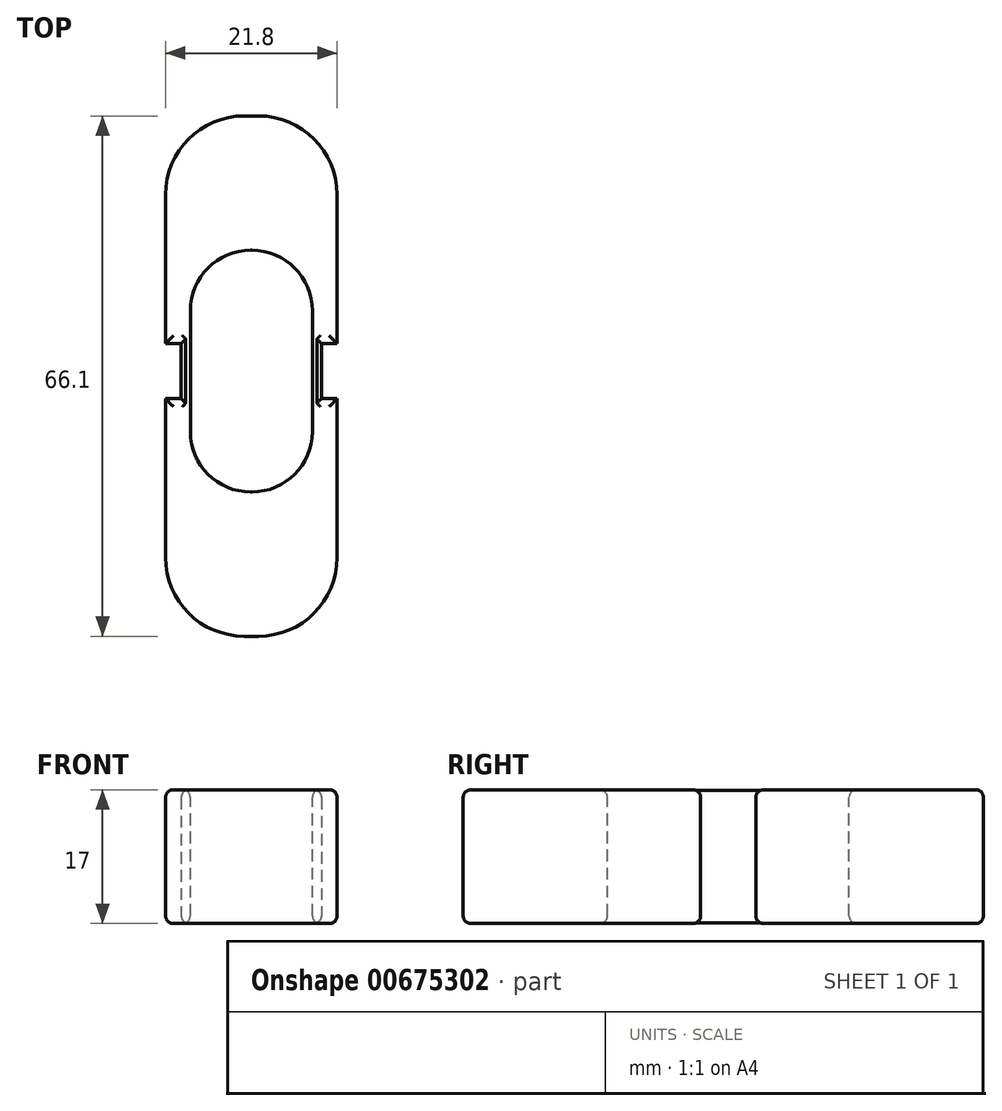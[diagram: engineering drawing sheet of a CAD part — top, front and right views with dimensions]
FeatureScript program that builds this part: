
annotation { "Feature Type Name" : "Feature", "Feature Type Description" : "" }
export const myFeature = defineFeature(function(context is Context, id is Id, definition is map)
    precondition{}
    {
        {
            var Q0;
            Q0=qCreatedBy(makeId("Top.planeOp"),FACE);
            var sketch = newSketch(context, id + "F0", { "sketchPlane" : qUnion([Q0])});
            skLineSegment(sketch, "E0.bottom", {"start": v(-10.9, 32.42) * mm, "end": v(10.9, 32.42) * mm});
            skLineSegment(sketch, "E0.top", {"start": v(-10.9, -33.68) * mm, "end": v(10.9, -33.68) * mm});
            skLineSegment(sketch, "E0.left", {"start": v(-10.9, 32.42) * mm, "end": v(-10.9, -33.68) * mm});
            skLineSegment(sketch, "E0.right", {"start": v(10.9, 32.42) * mm, "end": v(10.9, -33.68) * mm});
            skSolve(sketch);
        }
        {
            var Q0;
            Q0=makeQuery(id+"F0.imprint","IMPRINT",FACE,{"disambiguationData":[TD([[makeQuery(id+"F0.imprint","IMPRINT",EDGE,{"derivedFrom":sQuery(id+"F0.wireOp",EDGE,"E0.bottom")}),-1.0]])]});
            extrude(context, id + "F1", {"entities" : qUnion([Q0]), "depth" : 17 * mm, "offsetDistance" : 25 * mm});
        }
        {
            var Q0;
            Q0=makeQuery(id+"F1.opExtrude","CAP_FACE",FACE,{"disambiguationData":[OSD([sQuery(id+"F0.wireOp",EDGE,"E0.bottom"),sQuery(id+"F0.wireOp",EDGE,"E0.top"),sQuery(id+"F0.wireOp",EDGE,"E0.left"),sQuery(id+"F0.wireOp",EDGE,"E0.right")])],"isStart":false});
            var sketch = newSketch(context, id + "F2", { "sketchPlane" : qUnion([Q0])});
            skLineSegment(sketch, "E1.bottom", {"start": v(-7.75, 15.35) * mm, "end": v(7.75, 15.35) * mm});
            skLineSegment(sketch, "E1.top", {"start": v(-7.75, -15.35) * mm, "end": v(7.75, -15.35) * mm});
            skLineSegment(sketch, "E1.left", {"start": v(-7.75, 15.35) * mm, "end": v(-7.75, -15.35) * mm});
            skLineSegment(sketch, "E1.right", {"start": v(7.75, 15.35) * mm, "end": v(7.75, -15.35) * mm});
            skSolve(sketch);
        }
        {
            var Q0;
            Q0=makeQuery(id+"F2.imprint","IMPRINT",FACE,{"disambiguationData":[TD([[makeQuery(id+"F2.imprint","IMPRINT",EDGE,{"derivedFrom":sQuery(id+"F2.wireOp",EDGE,"E1.bottom")}),-1.0]])]});
            extrude(context, id + "F3", {"entities" : qUnion([Q0]), "operationType" : NewBodyOperationType.REMOVE, "oppositeDirection" : true, "depth" : 40 * mm, "offsetDistance" : 25 * mm});
        }
        {
            var Q0;
            Q0=makeQuery(id+"F1.opExtrude","SWEPT_EDGE",EDGE,{"disambiguationData":[OSD([sQuery(id+"F0.wireOp",EDGE,"E0.top"),sQuery(id+"F0.wireOp",EDGE,"E0.right")])]});
            var Q1;
            Q1=makeQuery(id+"F1.opExtrude","SWEPT_EDGE",EDGE,{"disambiguationData":[OSD([sQuery(id+"F0.wireOp",EDGE,"E0.top"),sQuery(id+"F0.wireOp",EDGE,"E0.left")])]});
            var Q2;
            Q2=makeQuery(id+"F1.opExtrude","SWEPT_EDGE",EDGE,{"disambiguationData":[OSD([sQuery(id+"F0.wireOp",EDGE,"E0.bottom"),sQuery(id+"F0.wireOp",EDGE,"E0.left")])]});
            var Q3;
            Q3=makeQuery(id+"F1.opExtrude","SWEPT_EDGE",EDGE,{"disambiguationData":[OSD([sQuery(id+"F0.wireOp",EDGE,"E0.bottom"),sQuery(id+"F0.wireOp",EDGE,"E0.right")])]});
            fillet(context, id + "F4", {"entities" : qUnion([Q0, Q1, Q2, Q3]), "radius" : 10 * mm, "tangentPropagation" : true, "allowEdgeOverflow" : false});
        }
        {
            var Q0;
            Q0=makeQuery(id+"F3.boolean.opBoolean","COPY",EDGE,{"derivedFrom":makeQuery(id+"F3.opExtrude","SWEPT_EDGE",EDGE,{"disambiguationData":[OSD([sQuery(id+"F2.wireOp",EDGE,"E1.bottom"),sQuery(id+"F2.wireOp",EDGE,"E1.left")])]})});
            var Q1;
            Q1=makeQuery(id+"F3.boolean.opBoolean","COPY",EDGE,{"derivedFrom":makeQuery(id+"F3.opExtrude","SWEPT_EDGE",EDGE,{"disambiguationData":[OSD([sQuery(id+"F2.wireOp",EDGE,"E1.bottom"),sQuery(id+"F2.wireOp",EDGE,"E1.right")])]})});
            var Q2;
            Q2=makeQuery(id+"F3.boolean.opBoolean","COPY",EDGE,{"derivedFrom":makeQuery(id+"F3.opExtrude","SWEPT_EDGE",EDGE,{"disambiguationData":[OSD([sQuery(id+"F2.wireOp",EDGE,"E1.top"),sQuery(id+"F2.wireOp",EDGE,"E1.left")])]})});
            var Q3;
            Q3=makeQuery(id+"F3.boolean.opBoolean","COPY",EDGE,{"derivedFrom":makeQuery(id+"F3.opExtrude","SWEPT_EDGE",EDGE,{"disambiguationData":[OSD([sQuery(id+"F2.wireOp",EDGE,"E1.top"),sQuery(id+"F2.wireOp",EDGE,"E1.right")])]})});
            fillet(context, id + "F5", {"entities" : qUnion([Q0, Q1, Q2, Q3]), "radius" : 7.65 * mm, "tangentPropagation" : true, "allowEdgeOverflow" : false});
        }
        {
            var Q0;
            Q0=makeQuery(id+"F1.opExtrude","CAP_FACE",FACE,{"disambiguationData":[OSD([sQuery(id+"F0.wireOp",EDGE,"E0.bottom"),sQuery(id+"F0.wireOp",EDGE,"E0.top"),sQuery(id+"F0.wireOp",EDGE,"E0.left"),sQuery(id+"F0.wireOp",EDGE,"E0.right")])],"isStart":true});
            var sketch = newSketch(context, id + "F6", { "sketchPlane" : qUnion([Q0])});
            skLineSegment(sketch, "E2.bottom", {"start": v(-10.9, 3.5) * mm, "end": v(-8.9, 3.5) * mm});
            skLineSegment(sketch, "E2.top", {"start": v(-10.9, -3.5) * mm, "end": v(-8.9, -3.5) * mm});
            skLineSegment(sketch, "E2.left", {"start": v(-10.9, 3.5) * mm, "end": v(-10.9, -3.5) * mm});
            skLineSegment(sketch, "E2.right", {"start": v(-8.9, 3.5) * mm, "end": v(-8.9, -3.5) * mm});
            skLineSegment(sketch, "E3.MirrorCS", {"start": v(10.9, -3.5) * mm, "end": v(8.9, -3.5) * mm});
            skLineSegment(sketch, "E4.MirrorCS", {"start": v(10.9, 3.5) * mm, "end": v(8.9, 3.5) * mm});
            skLineSegment(sketch, "E5.MirrorCS", {"start": v(10.9, 3.5) * mm, "end": v(10.9, -3.5) * mm});
            skLineSegment(sketch, "E6.MirrorCS", {"start": v(8.9, 3.5) * mm, "end": v(8.9, -3.5) * mm});
            skSolve(sketch);
        }
        {
            var Q0;
            Q0=makeQuery(id+"F6.imprint","IMPRINT",FACE,{"disambiguationData":[TD([[makeQuery(id+"F6.imprint","IMPRINT",EDGE,{"derivedFrom":sQuery(id+"F6.wireOp",EDGE,"E2.bottom")}),-1.0]])]});
            var Q1;
            Q1=makeQuery(id+"F6.imprint","IMPRINT",FACE,{"disambiguationData":[TD([[makeQuery(id+"F6.imprint","IMPRINT",EDGE,{"derivedFrom":sQuery(id+"F6.wireOp",EDGE,"E3.MirrorCS")}),-1.0]])]});
            extrude(context, id + "F7", {"entities" : qUnion([Q0, Q1]), "operationType" : NewBodyOperationType.REMOVE, "oppositeDirection" : true, "depth" : 20 * mm, "offsetDistance" : 25 * mm});
        }
        {
            var Q0;
            Q0=makeQuery(id+"F1.opExtrude","CAP_FACE",FACE,{"disambiguationData":[OSD([sQuery(id+"F0.wireOp",EDGE,"E0.bottom"),sQuery(id+"F0.wireOp",EDGE,"E0.top"),sQuery(id+"F0.wireOp",EDGE,"E0.left"),sQuery(id+"F0.wireOp",EDGE,"E0.right")])],"isStart":false});
            var Q1;
            Q1=makeQuery(id+"F1.opExtrude","CAP_FACE",FACE,{"disambiguationData":[OSD([sQuery(id+"F0.wireOp",EDGE,"E0.bottom"),sQuery(id+"F0.wireOp",EDGE,"E0.top"),sQuery(id+"F0.wireOp",EDGE,"E0.left"),sQuery(id+"F0.wireOp",EDGE,"E0.right")])],"isStart":true});
            fillet(context, id + "F8", {"entities" : qUnion([Q0, Q1]), "radius" : 1 * mm, "tangentPropagation" : true, "allowEdgeOverflow" : false});
        }
    });
